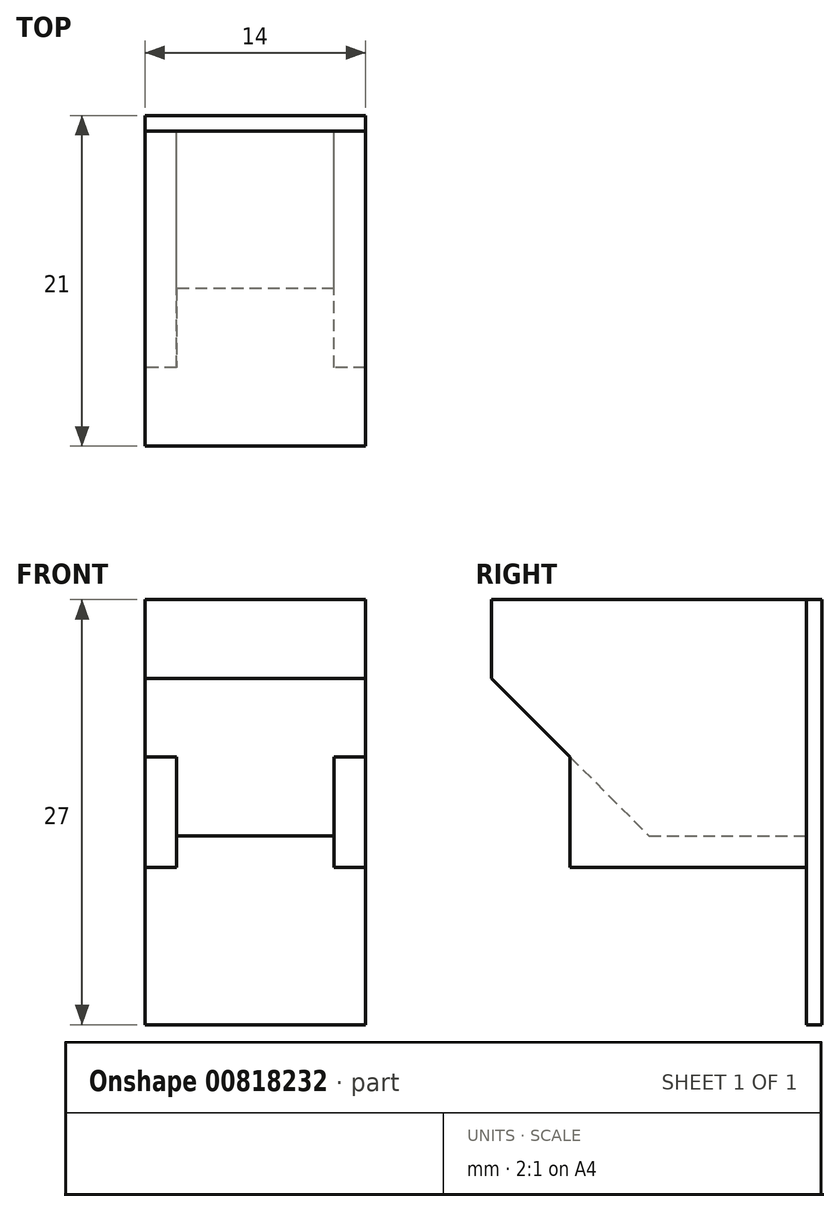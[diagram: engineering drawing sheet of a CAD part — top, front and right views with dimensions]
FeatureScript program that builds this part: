
annotation { "Feature Type Name" : "Feature", "Feature Type Description" : "" }
export const myFeature = defineFeature(function(context is Context, id is Id, definition is map)
    precondition{}
    {
        {
            var Q0;
            Q0=qCreatedBy(makeId("Top.planeOp"),FACE);
            var sketch = newSketch(context, id + "F0", { "sketchPlane" : qUnion([Q0])});
            skLineSegment(sketch, "E0.bottom", {"start": v(7, -10) * mm, "end": v(-7, -10) * mm});
            skLineSegment(sketch, "E0.top", {"start": v(7, 10) * mm, "end": v(-7, 10) * mm});
            skLineSegment(sketch, "E0.left", {"start": v(7, -10) * mm, "end": v(7, 10) * mm});
            skLineSegment(sketch, "E0.right", {"start": v(-7, -10) * mm, "end": v(-7, 10) * mm});
            skPoint(sketch, "E0.middle", {"position": v(0, 0) * mm});
            skSolve(sketch);
        }
        {
            var Q0;
            Q0 = qSketchRegion(id + "F0", true);
            extrude(context, id + "F1", {"entities" : qUnion([Q0]), "depth" : 15 * mm, "offsetDistance" : 25 * mm});
        }
        {
            var Q0;
            Q0=qCreatedBy(makeId("Top.planeOp"),FACE);
            var sketch = newSketch(context, id + "F2", { "sketchPlane" : qUnion([Q0])});
            skLineSegment(sketch, "E1.bottom", {"start": v(7, -5) * mm, "end": v(5, -5) * mm});
            skLineSegment(sketch, "E1.top", {"start": v(7, 10) * mm, "end": v(5, 10) * mm});
            skLineSegment(sketch, "E1.left", {"start": v(7, -5) * mm, "end": v(7, 10) * mm});
            skLineSegment(sketch, "E1.right", {"start": v(5, -5) * mm, "end": v(5, 10) * mm});
            skPoint(sketch, "E1.middle", {"position": v(6, 2.5) * mm});
            skLineSegment(sketch, "E2.1.0.0", {"start": v(-7, -5) * mm, "end": v(-7, 10) * mm});
            skLineSegment(sketch, "E2.1.0.1", {"start": v(-5, -5) * mm, "end": v(-5, 10) * mm});
            skLineSegment(sketch, "E2.1.0.2", {"start": v(-5, 10) * mm, "end": v(-7, 10) * mm});
            skLineSegment(sketch, "E2.1.0.3", {"start": v(-5, -5) * mm, "end": v(-7, -5) * mm});
            skPoint(sketch, "E2.1.0.4", {"position": v(-6, 2.5) * mm});
            skLineSegment(sketch, "E2.direction1", {"start": v(-7, -5) * mm, "end": v(5, -5) * mm, "construction": true});
            skSolve(sketch);
        }
        {
            var Q0;
            Q0 = qSketchRegion(id + "F2", true);
            extrude(context, id + "F3", {"entities" : qUnion([Q0]), "operationType" : NewBodyOperationType.ADD, "endBound" : BoundingType.SYMMETRIC, "oppositeDirection" : true, "depth" : 4 * mm, "offsetDistance" : 25 * mm});
        }
        {
            var Q0;
            Q0=qCreatedBy(makeId("Top.planeOp"),FACE);
            var sketch = newSketch(context, id + "F4", { "sketchPlane" : qUnion([Q0])});
            skLineSegment(sketch, "E3.bottom", {"start": v(7, 10) * mm, "end": v(-7, 10) * mm});
            skLineSegment(sketch, "E3.top", {"start": v(7, 11) * mm, "end": v(-7, 11) * mm});
            skLineSegment(sketch, "E3.left", {"start": v(7, 10) * mm, "end": v(7, 11) * mm});
            skLineSegment(sketch, "E3.right", {"start": v(-7, 10) * mm, "end": v(-7, 11) * mm});
            skPoint(sketch, "E3.middle", {"position": v(0, 10.5) * mm});
            skSolve(sketch);
        }
        {
            var Q0;
            Q0 = qSketchRegion(id + "F4", true);
            extrude(context, id + "F5", {"entities" : qUnion([Q0]), "oppositeDirection" : true, "depth" : 27 * mm, "offsetDistance" : 25 * mm});
        }
        {
            var Q0;
            Q0=makeQuery(id+"F5.opExtrude","SWEPT_BODY",BODY,{"disambiguationData":[OSD([sQuery(id+"F4.wireOp",EDGE,"E3.bottom"),sQuery(id+"F4.wireOp",EDGE,"E3.top"),sQuery(id+"F4.wireOp",EDGE,"E3.left"),sQuery(id+"F4.wireOp",EDGE,"E3.right")])]});
            transform(context, id + "F6", {"entities" : qUnion([Q0]), "transformType" : TransformType.TRANSLATION_3D, "dx" : 0 * mm, "dy" : 0 * mm, "dz" : 15 * mm, "makeCopy" : false});
        }
        {
            var Q0;
            Q0=makeQuery(id+"F1.opExtrude","CAP_EDGE",EDGE,{"disambiguationData":[OSD([sQuery(id+"F0.wireOp",EDGE,"E0.bottom")])],"isStart":true});
            chamfer(context, id + "F7", {"entities" : qUnion([Q0]), "width" : 10 * mm, "tangentPropagation" : true});
        }
    });
